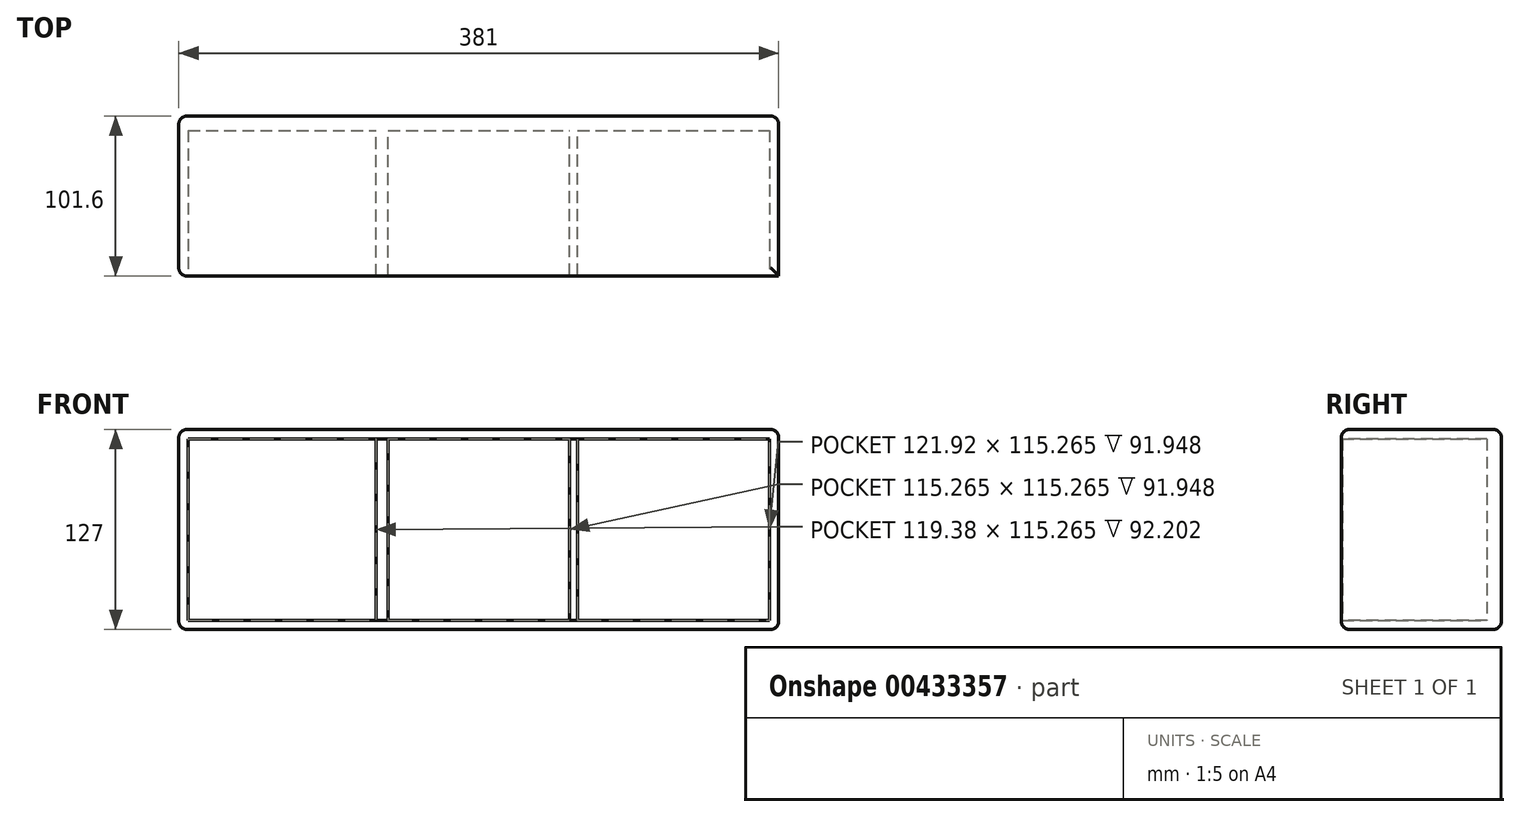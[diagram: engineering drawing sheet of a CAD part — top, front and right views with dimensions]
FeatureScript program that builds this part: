
annotation { "Feature Type Name" : "Feature", "Feature Type Description" : "" }
export const myFeature = defineFeature(function(context is Context, id is Id, definition is map)
    precondition{}
    {
        {
            var Q0;
            Q0=qCreatedBy(makeId("Top.planeOp"),FACE);
            var sketch = newSketch(context, id + "F0", { "sketchPlane" : qUnion([Q0])});
            skLineSegment(sketch, "E0.bottom", {"start": v(-190.5, 50.8) * mm, "end": v(190.5, 50.8) * mm});
            skLineSegment(sketch, "E0.top", {"start": v(-190.5, -50.8) * mm, "end": v(190.5, -50.8) * mm});
            skLineSegment(sketch, "E0.left", {"start": v(-190.5, 50.8) * mm, "end": v(-190.5, -50.8) * mm});
            skLineSegment(sketch, "E0.right", {"start": v(190.5, 50.8) * mm, "end": v(190.5, -50.8) * mm});
            skPoint(sketch, "E0.middle", {"position": v(0, 0) * mm});
            skSolve(sketch);
        }
        {
            var Q0;
            Q0=makeQuery(id+"F0.imprint","IMPRINT",FACE,{"disambiguationData":[TD([[makeQuery(id+"F0.imprint","IMPRINT",EDGE,{"derivedFrom":sQuery(id+"F0.wireOp",EDGE,"E0.bottom")}),-1.0]])]});
            extrude(context, id + "F1", {"entities" : qUnion([Q0]), "depth" : 127 * mm});
        }
        {
            var Q0;
            Q0=makeQuery(id+"F1.opExtrude","SWEPT_FACE",FACE,{"disambiguationData":[OSD([sQuery(id+"F0.wireOp",EDGE,"E0.top")])]});
            var sketch = newSketch(context, id + "F2", { "sketchPlane" : qUnion([Q0])});
            skLineSegment(sketch, "E1.bottom", {"start": v(-184.63, 121.13) * mm, "end": v(184.63, 121.13) * mm});
            skLineSegment(sketch, "E1.top", {"start": v(-184.63, 5.87) * mm, "end": v(184.63, 5.87) * mm});
            skLineSegment(sketch, "E1.left", {"start": v(-184.63, 121.13) * mm, "end": v(-184.63, 5.87) * mm});
            skLineSegment(sketch, "E1.right", {"start": v(184.63, 121.13) * mm, "end": v(184.63, 5.87) * mm});
            skSolve(sketch);
        }
        {
            var Q0;
            Q0=makeQuery(id+"F2.imprint","IMPRINT",FACE,{"disambiguationData":[TD([[makeQuery(id+"F2.imprint","IMPRINT",EDGE,{"derivedFrom":sQuery(id+"F2.wireOp",EDGE,"E1.bottom")}),-1.0]])]});
            extrude(context, id + "F3", {"entities" : qUnion([Q0]), "operationType" : NewBodyOperationType.REMOVE, "oppositeDirection" : true, "depth" : 92.46 * mm});
        }
        {
            var Q0;
            Q0=makeQuery(id+"F3.boolean.opBoolean","COPY",FACE,{"derivedFrom":makeQuery(id+"F3.opExtrude","CAP_FACE",FACE,{"disambiguationData":[OSD([sQuery(id+"F2.wireOp",EDGE,"E1.bottom"),sQuery(id+"F2.wireOp",EDGE,"E1.top"),sQuery(id+"F2.wireOp",EDGE,"E1.left"),sQuery(id+"F2.wireOp",EDGE,"E1.right")])],"isStart":false})});
            var sketch = newSketch(context, id + "F4", { "sketchPlane" : qUnion([Q0])});
            skLineSegment(sketch, "E2.bottom", {"start": v(-57.63, 121.13) * mm, "end": v(-65.25, 121.13) * mm});
            skLineSegment(sketch, "E2.top", {"start": v(-57.63, 5.87) * mm, "end": v(-65.25, 5.87) * mm});
            skLineSegment(sketch, "E2.left", {"start": v(-65.25, 121.13) * mm, "end": v(-65.25, 5.87) * mm});
            skLineSegment(sketch, "E2.right", {"start": v(-57.63, 121.13) * mm, "end": v(-57.63, 5.87) * mm});
            skSolve(sketch);
        }
        {
            var Q0;
            Q0 = qSketchRegion(id + "F4", true);
            extrude(context, id + "F5", {"entities" : qUnion([Q0]), "operationType" : NewBodyOperationType.ADD, "depth" : 92.2 * mm});
        }
        {
            var Q0;
            {var subQ0=sQuery(id+"F2.wireOp",EDGE,"E1.bottom");var subQ1=sQuery(id+"F2.wireOp",EDGE,"E1.top");var subQ2=sQuery(id+"F2.wireOp",EDGE,"E1.right");Q0=makeQuery(id+"F5.boolean.opBoolean","SPLIT",FACE,{"disambiguationData":[TD([makeQuery(id+"F3.boolean.opBoolean","COPY",FACE,{"derivedFrom":makeQuery(id+"F3.opExtrude","SWEPT_FACE",FACE,{"disambiguationData":[OSD([subQ2])]})})])],"derivedFrom":makeQuery(id+"F3.boolean.opBoolean","COPY",FACE,{"derivedFrom":makeQuery(id+"F3.opExtrude","CAP_FACE",FACE,{"disambiguationData":[OSD([subQ0,subQ1,sQuery(id+"F2.wireOp",EDGE,"E1.left"),subQ2])],"isStart":false})})});}
            var sketch = newSketch(context, id + "F6", { "sketchPlane" : qUnion([Q0])});
            skLineSegment(sketch, "E3.bottom", {"start": v(62.71, 121.13) * mm, "end": v(57.63, 121.13) * mm});
            skLineSegment(sketch, "E3.top", {"start": v(62.71, 5.87) * mm, "end": v(57.63, 5.87) * mm});
            skLineSegment(sketch, "E3.left", {"start": v(57.63, 121.13) * mm, "end": v(57.63, 5.87) * mm});
            skLineSegment(sketch, "E3.right", {"start": v(62.71, 121.13) * mm, "end": v(62.71, 5.87) * mm});
            skSolve(sketch);
        }
        {
            var Q0;
            Q0=makeQuery(id+"F6.imprint","IMPRINT",FACE,{"disambiguationData":[TD([[makeQuery(id+"F6.imprint","IMPRINT",EDGE,{"derivedFrom":sQuery(id+"F6.wireOp",EDGE,"E3.bottom")}),-1.0]])]});
            var Q1;
            Q1=sQuery(id+"F6.wireOp",EDGE,"E3.left");
            var Q2;
            Q2=sQuery(id+"F6.wireOp",EDGE,"E3.right");
            extrude(context, id + "F7", {"entities" : qUnion([Q0]), "operationType" : NewBodyOperationType.ADD, "surfaceEntities" : qUnion([Q1, Q2]), "depth" : 91.95 * mm});
        }
        {
            var Q0;
            Q0=makeQuery(id+"F1.opExtrude","CAP_FACE",FACE,{"disambiguationData":[OSD([sQuery(id+"F0.wireOp",EDGE,"E0.bottom"),sQuery(id+"F0.wireOp",EDGE,"E0.top"),sQuery(id+"F0.wireOp",EDGE,"E0.left"),sQuery(id+"F0.wireOp",EDGE,"E0.right")])],"isStart":true});
            var Q1;
            Q1=makeQuery(id+"F1.opExtrude","SWEPT_FACE",FACE,{"disambiguationData":[OSD([sQuery(id+"F0.wireOp",EDGE,"E0.left")])]});
            fillet(context, id + "F8", {"entities" : qUnion([Q0, Q1]), "radius" : 5.08 * mm, "tangentPropagation" : true, "allowEdgeOverflow" : false});
        }
        {
            var Q0;
            Q0=makeQuery(id+"F1.opExtrude","CAP_FACE",FACE,{"disambiguationData":[OSD([sQuery(id+"F0.wireOp",EDGE,"E0.bottom"),sQuery(id+"F0.wireOp",EDGE,"E0.top"),sQuery(id+"F0.wireOp",EDGE,"E0.left"),sQuery(id+"F0.wireOp",EDGE,"E0.right")])],"isStart":false});
            var Q1;
            Q1=makeQuery(id+"F1.opExtrude","SWEPT_FACE",FACE,{"disambiguationData":[OSD([sQuery(id+"F0.wireOp",EDGE,"E0.bottom")])]});
            fillet(context, id + "F9", {"entities" : qUnion([Q0, Q1]), "radius" : 5.08 * mm, "tangentPropagation" : true, "allowEdgeOverflow" : false});
        }
    });
